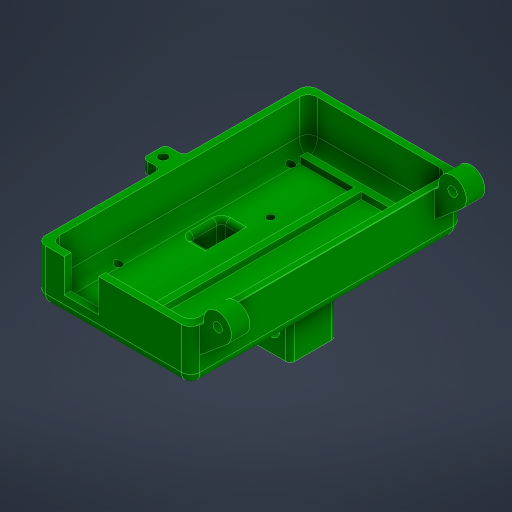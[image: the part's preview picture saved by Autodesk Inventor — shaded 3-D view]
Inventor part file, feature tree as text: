
AUTODESK INVENTOR PART (.ipt)
format: ipt  version: 2024 (Build 280153000, 153)  size: 613,888 bytes
history: native  units: mm
features: other x18, reference x12, sketch x11, extrude x11, fillet x6, mirror x2, projected_geometry x2
ambient origin geometry x8: Origin, YZ Plane, XZ Plane, XY Plane, X Axis, Y Axis, Z Axis, Center Point
bodies: Body1 (feature_tree)
feature tree (62):
  other  "Твердое тело1"
  sketch  "Эскиз1"
  other  "РабПлоскость1"
  extrude  "Выдавливание1"  Depth=15.0mm
  extrude  "Выдавливание2"  Depth=15.0mm
  extrude  "Выдавливание3"  Depth=3.0mm
  extrude  "Выдавливание4"  Depth=10.0mm TaperAngle=0.0deg
  fillet  "Сопряжение3"  Radius=3.0mm
  extrude  "Выдавливание5"  Depth=3.0mm
  extrude  "Выдавливание6"  Depth=3.0mm
  other  "Непосредственное редактирование1"
  extrude  "Выдавливание7"  Depth=17.0mm TaperAngle=0.0deg
  fillet  "Сопряжение5"  Radius=3.0mm
  fillet  "Сопряжение6"  Radius=3.0mm
  other  "РабПлоскость3"
  extrude  "Выдавливание10"  Depth=3.0mm
  other  "РабПлоскость6"
  mirror  "Зеркальное отражение1"
  fillet  "Сопряжение7"  Radius=20.0mm
  other  "РабПлоскость7"
  extrude  "Выдавливание11"  Depth=4.0mm
  fillet  "Сопряжение8"  Radius=3.0mm
  fillet  "Сопряжение9"  Radius=6.0mm
  extrude  "Выдавливание12"  Depth=50.0mm
  extrude  "Выдавливание13"  Depth=3.0mm
  other  "РабПлоскость8"
  mirror  "Зеркальное отражение2"
  reference  "Ссылка1"
  reference  "Ссылка2"
  reference  "Ссылка3"
  reference  "Ссылка4"
  sketch  "Эскиз2"
  sketch  "Эскиз3"
  sketch  "Эскиз4"
  sketch  "Эскиз9"
  sketch  "Эскиз10"
  reference  "Ссылка5"
  reference  "Ссылка6"
  reference  "Ссылка7"
  reference  "Ссылка8"
  reference  "Ссылка9"
  reference  "Ссылка10"
  sketch  "Эскиз11"
  sketch  "Эскиз15"
  sketch  "Эскиз17"
  reference  "Ссылка20"
  reference  "Ссылка21"
  projected_geometry  "Спроецированная петля1"
  projected_geometry  "Спроецированная петля2"
  sketch  "Эскиз18"
  sketch  "Эскиз19"
  parser-record x2  (decoder bookkeeping rows leaked as tree rows — omitted from the tree; the rows remain in map.json)
  other  "main_assembly.iam"
  other  "base_assembly:1"
  other  "section:4"
  other  "main axis:1"
  other  "Arduino MEGA 2560 R3:1"
  other  "Перенос1"
  other  "shock_absorber_holder_down_200:1"
  other  "front_box.iam"
  other  "front_box_cup:1"
note: 2 file-system paths scrubbed to <path> (originals preserved in map.json)
